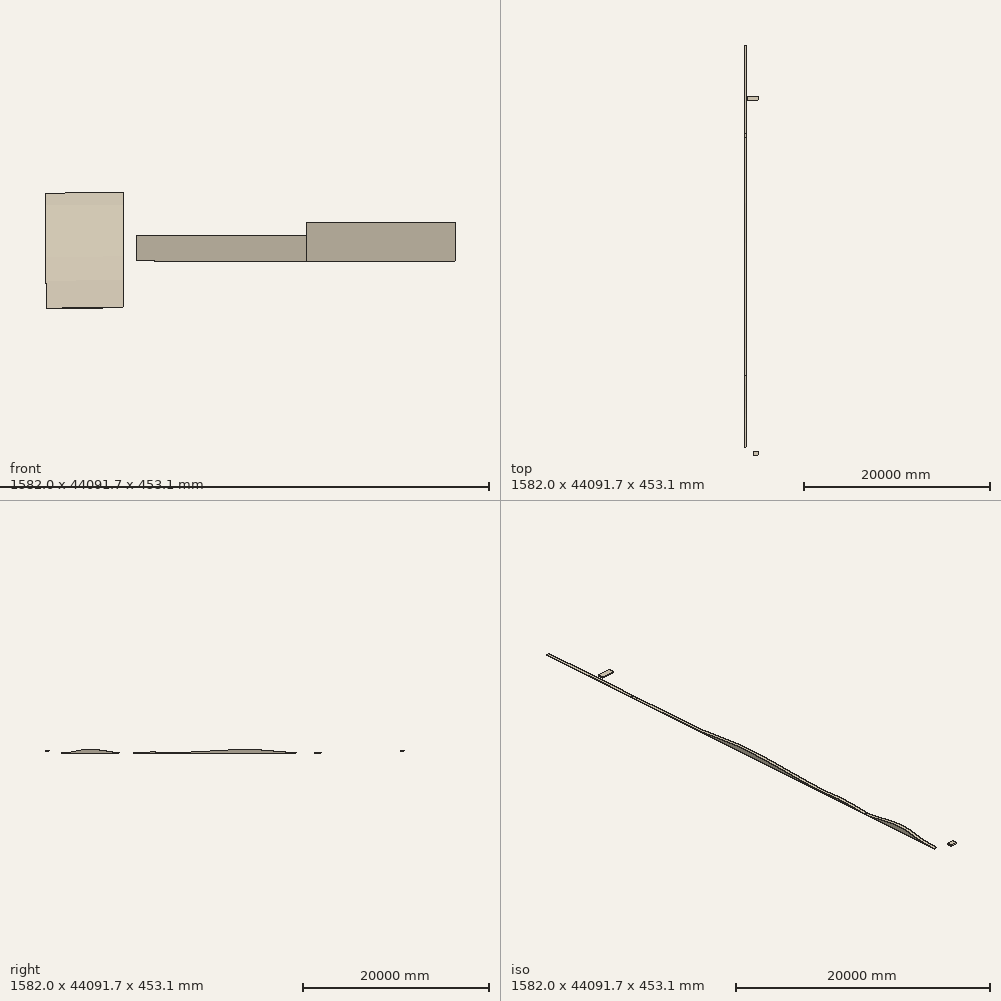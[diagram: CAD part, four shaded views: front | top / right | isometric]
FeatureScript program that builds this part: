
annotation { "Feature Type Name" : "Feature", "Feature Type Description" : "" }
export const myFeature = defineFeature(function(context is Context, id is Id, definition is map)
    precondition{}
    {
        {
            var Q0;
            Q0=qCreatedBy(makeId("Front.planeOp"),FACE);
            var sketch = newSketch(context, id + "F0", { "sketchPlane" : qUnion([Q0])});
            skLineSegment(sketch, "E0", {"start": v(-127.06, 0) * mm, "end": v(164.32, 0) * mm});
            skLineSegment(sketch, "E1", {"start": v(194.32, -30) * mm, "end": v(194.32, -179.95) * mm});
            skLineSegment(sketch, "E2", {"start": v(194.32, -179.95) * mm, "end": v(544.31, -177.98) * mm});
            skLineSegment(sketch, "E3", {"start": v(544.31, -177.98) * mm, "end": v(543.46, -28) * mm});
            skLineSegment(sketch, "E4", {"start": v(573.52, 2.18) * mm, "end": v(1823.51, 0.05) * mm});
            skLineSegment(sketch, "E5", {"start": v(1853.46, -29.78) * mm, "end": v(1854.3, -177.98) * mm});
            skLineSegment(sketch, "E6", {"start": v(1854.3, -177.98) * mm, "end": v(2204.3, -176) * mm});
            skLineSegment(sketch, "E7", {"start": v(2204.3, -176) * mm, "end": v(2203.58, -50) * mm});
            skLineSegment(sketch, "E8", {"start": v(2253.3, 0.28) * mm, "end": v(2454.27, 1.42) * mm});
            skPoint(sketch, "E9.visualSharp", {"position": v(2203.3, 0) * mm});
            skArc(sketch, "E9.filletArc", {"start": v(2253.3, 0.28) * mm, "mid": v(2218.03, -14.56) * mm, "end": v(2203.58, -50) * mm});
            skPoint(sketch, "E10.visualSharp", {"position": v(1853.3, 0) * mm});
            skArc(sketch, "E10.filletArc", {"start": v(1853.46, -29.78) * mm, "mid": v(1844.63, -8.7) * mm, "end": v(1823.51, 0.05) * mm});
            skPoint(sketch, "E11.visualSharp", {"position": v(543.3, 2.23) * mm});
            skArc(sketch, "E11.filletArc", {"start": v(573.52, 2.18) * mm, "mid": v(552.2, -6.65) * mm, "end": v(543.46, -28) * mm});
            skPoint(sketch, "E12.visualSharp", {"position": v(194.32, 0) * mm});
            skArc(sketch, "E12.filletArc", {"start": v(194.32, -30) * mm, "mid": v(185.53, -8.79) * mm, "end": v(164.32, 0) * mm});
            skSolve(sketch);
        }
        {
            var Q0;
            Q0=sQuery(id+"F0.wireOp",EDGE,"E0");
            var Q1;
            Q1=sQuery(id+"F0.wireOp",EDGE,"E1");
            var Q2;
            Q2=sQuery(id+"F0.wireOp",EDGE,"E2");
            var Q3;
            Q3=sQuery(id+"F0.wireOp",EDGE,"E3");
            var Q4;
            Q4=sQuery(id+"F0.wireOp",EDGE,"E4");
            var Q5;
            Q5=sQuery(id+"F0.wireOp",EDGE,"E5");
            var Q6;
            Q6=sQuery(id+"F0.wireOp",EDGE,"E6");
            var Q7;
            Q7=sQuery(id+"F0.wireOp",EDGE,"E7");
            var Q8;
            Q8=sQuery(id+"F0.wireOp",EDGE,"E8");
            var Q9;
            Q9=sQuery(id+"F0.wireOp",EDGE,"E9.filletArc");
            var Q10;
            Q10=sQuery(id+"F0.wireOp",EDGE,"E10.filletArc");
            var Q11;
            Q11=sQuery(id+"F0.wireOp",EDGE,"E11.filletArc");
            var Q12;
            Q12=sQuery(id+"F0.wireOp",EDGE,"E12.filletArc");
            extrude(context, id + "F1", {"bodyType" : ToolBodyType.SURFACE, "surfaceEntities" : qUnion([Q0, Q1, Q2, Q3, Q4, Q5, Q6, Q7, Q8, Q9, Q10, Q11, Q12]), "depth" : 80000 * mm, "offsetDistance" : 25 * mm});
        }
        {
            var Q0;
            Q0=makeQuery(id+"F1.opExtrude","SWEPT_FACE",FACE,{"disambiguationData":[OSD([sQuery(id+"F0.wireOp",EDGE,"E3")])]});
            var sketch = newSketch(context, id + "F2", { "sketchPlane" : qUnion([Q0])});
            skLineSegment(sketch, "E13", {"start": v(0, -181.05) * mm, "end": v(0, 0) * mm});
            skLineSegment(sketch, "E14", {"start": v(0, -181.05) * mm, "end": v(-43231.56, -181.05) * mm});
            skPoint(sketch, "E15.2.internal.snap0", {"position": v(-40000, -181.05) * mm});
            skFitSpline(sketch, "E15", {"points": [v(-43231.56, -181.05) * mm, v(-41346.3, -31.06) * mm, v(-40000, 235.08) * mm, v(-38081.96, 183.26) * mm, v(-36855.67, -31.06) * mm, v(-36216.63, -110.36) * mm, v(-35456.67, -181.05) * mm, v(-33487.7, -31.06) * mm, v(-31691.46, -31.06) * mm, v(-30309.73, -101.72) * mm, v(-21861.42, 248.3) * mm, v(-17358.5, -116.28) * mm, v(-15464.68, -125.3) * mm, v(-12475.16, -138.82) * mm, v(-9413.5, -181.05) * mm, v(-7654.96, -138.82) * mm, v(0, -181.05) * mm], "startDerivative": vector(35839.75, 1484.64) * mm, "endDerivative": vector(81398.05, -896.64) * mm});
            skSolve(sketch);
        }
        {
            var Q0;
            Q0 = qSketchRegion(id + "F2", true);
            extrude(context, id + "F3", {"entities" : qUnion([Q0]), "oppositeDirection" : true, "depth" : 300 * mm, "offsetDistance" : 25 * mm});
        }
        {
            var Q0;
            Q0=makeQuery(id+"F1.opExtrude","SWEPT_FACE",FACE,{"disambiguationData":[OSD([sQuery(id+"F0.wireOp",EDGE,"E4")])]});
            var sketch = newSketch(context, id + "F4", { "sketchPlane" : qUnion([Q0])});
            skLineSegment(sketch, "E16.bottom", {"start": v(573.51, 7714.69) * mm, "end": v(1823.51, 7714.69) * mm});
            skLineSegment(sketch, "E16.top", {"start": v(573.51, 7252.04) * mm, "end": v(1823.51, 7252.04) * mm});
            skLineSegment(sketch, "E16.left", {"start": v(573.51, 7714.69) * mm, "end": v(573.51, 7252.04) * mm});
            skLineSegment(sketch, "E16.right", {"start": v(1823.51, 7714.69) * mm, "end": v(1823.51, 7252.04) * mm});
            skLineSegment(sketch, "E17.bottom", {"start": v(1823.51, 43708.44) * mm, "end": v(1250.06, 43708.44) * mm});
            skLineSegment(sketch, "E17.top", {"start": v(1823.51, 44091.72) * mm, "end": v(1250.06, 44091.72) * mm});
            skLineSegment(sketch, "E17.left", {"start": v(1823.51, 43708.44) * mm, "end": v(1823.51, 44091.72) * mm});
            skLineSegment(sketch, "E17.right", {"start": v(1250.06, 43708.44) * mm, "end": v(1250.06, 44091.72) * mm});
            skSolve(sketch);
        }
        {
            var Q0;
            Q0=makeQuery(id+"F4.imprint","IMPRINT",FACE,{"disambiguationData":[TD([[makeQuery(id+"F4.imprint","IMPRINT",EDGE,{"derivedFrom":sQuery(id+"F4.wireOp",EDGE,"E17.bottom")}),-1.0]])]});
            extrude(context, id + "F5", {"entities" : qUnion([Q0]), "oppositeDirection" : true, "depth" : 150 * mm, "offsetDistance" : 25 * mm});
        }
        {
            var Q0;
            Q0=makeQuery(id+"F1.opExtrude","SWEPT_FACE",FACE,{"disambiguationData":[OSD([sQuery(id+"F0.wireOp",EDGE,"E4")])]});
            var sketch = newSketch(context, id + "F6", { "sketchPlane" : qUnion([Q0])});
            skSolve(sketch);
        }
        {
            var Q0;
            Q0=makeQuery(id+"F6.imprint","IMPRINT",FACE,{"disambiguationData":[TD([[makeQuery(id+"F6.imprint","IMPRINT",EDGE,{"derivedFrom":makeQuery(id+"F1.opExtrude","SWEPT_EDGE",EDGE,{"disambiguationData":[OSD([sQuery(id+"F0.wireOp",VERTEX,"E10.filletArc.end")])]})}),1.0]])]});
            var sketch = newSketch(context, id + "F7", { "sketchPlane" : qUnion([Q0])});
            skLineSegment(sketch, "E18.bottom", {"start": v(593.93, 5451.13) * mm, "end": v(1802.1, 5451.13) * mm});
            skLineSegment(sketch, "E18.top", {"start": v(593.93, 5926.07) * mm, "end": v(1802.1, 5926.07) * mm});
            skLineSegment(sketch, "E18.left", {"start": v(593.93, 5451.13) * mm, "end": v(593.93, 5926.07) * mm});
            skLineSegment(sketch, "E18.right", {"start": v(1802.1, 5451.13) * mm, "end": v(1802.1, 5926.07) * mm});
            skSolve(sketch);
        }
        {
            var Q0;
            Q0=makeQuery(id+"F7.imprint","IMPRINT",FACE,{"disambiguationData":[TD([[makeQuery(id+"F7.imprint","IMPRINT",EDGE,{"derivedFrom":sQuery(id+"F7.wireOp",EDGE,"E18.bottom")}),1.0]])]});
            extrude(context, id + "F8", {"entities" : qUnion([Q0]), "oppositeDirection" : true, "depth" : 100 * mm, "offsetDistance" : 25 * mm});
        }
        {
            var Q0;
            Q0=makeQuery(id+"F5.opExtrude","SWEPT_FACE",FACE,{"disambiguationData":[OSD([sQuery(id+"F4.wireOp",EDGE,"E17.top")])]});
            var sketch = newSketch(context, id + "F9", { "sketchPlane" : qUnion([Q0])});
            skLineSegment(sketch, "E19", {"start": v(2452.01, 0) * mm, "end": v(2770.17, 510.84) * mm});
            skLineSegment(sketch, "E20", {"start": v(3161.18, 510.84) * mm, "end": v(3161.18, -169.19) * mm});
            skLineSegment(sketch, "E21", {"start": v(3161.18, 510.84) * mm, "end": v(2770.17, 510.84) * mm});
            skSolve(sketch);
        }
        {
            var Q0;
            Q0=sQuery(id+"F9.wireOp",EDGE,"E21");
            var Q1;
            Q1=sQuery(id+"F9.wireOp",EDGE,"E19");
            var Q2;
            Q2=sQuery(id+"F9.wireOp",EDGE,"E20");
            extrude(context, id + "F10", {"bodyType" : ToolBodyType.SURFACE, "surfaceEntities" : qUnion([Q0, Q1, Q2]), "depth" : 17000 * mm, "offsetDistance" : 25 * mm});
        }
    });
